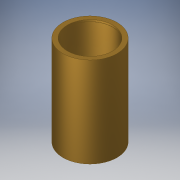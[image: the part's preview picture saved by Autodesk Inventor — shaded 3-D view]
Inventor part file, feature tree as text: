
AUTODESK INVENTOR PART (.ipt)
format: ipt  version: 2018 (Build 220112000, 112)  size: 117,760 bytes
history: native  units: in
note: dims shown in document units (in); Inventor stores cm internally (conversion verified against a paired STEP export)
features: extrude x4, sketch x4
ambient origin geometry x8: Origin, YZ Plane, XZ Plane, XY Plane, X Axis, Y Axis, Z Axis, Center Point
bodies: Solid1 (feature_tree)
feature tree (8):
  extrude  "Extrusion1"  Depth=1.0in TaperAngle=0.0deg
  extrude  "Extrusion2"  Depth=1.0in TaperAngle=0.0deg
  extrude  "Extrusion3"  Depth=0.02in TaperAngle=0.0deg
  extrude  "Extrusion4"  Depth=0.02in TaperAngle=0.0deg
  sketch  "Sketch1"  dims[d0=0.6in d1=1.0in d2=0.0in]
  sketch  "Sketch2"  dims[d3=0.5in d4=1.0in d5=0.0in]
  sketch  "Sketch3"  dims[d6=0.502in d7=0.02in d8=0.0in]
  sketch  "Sketch4"  dims[d9=0.502in d10=0.02in d11=0.0in]
